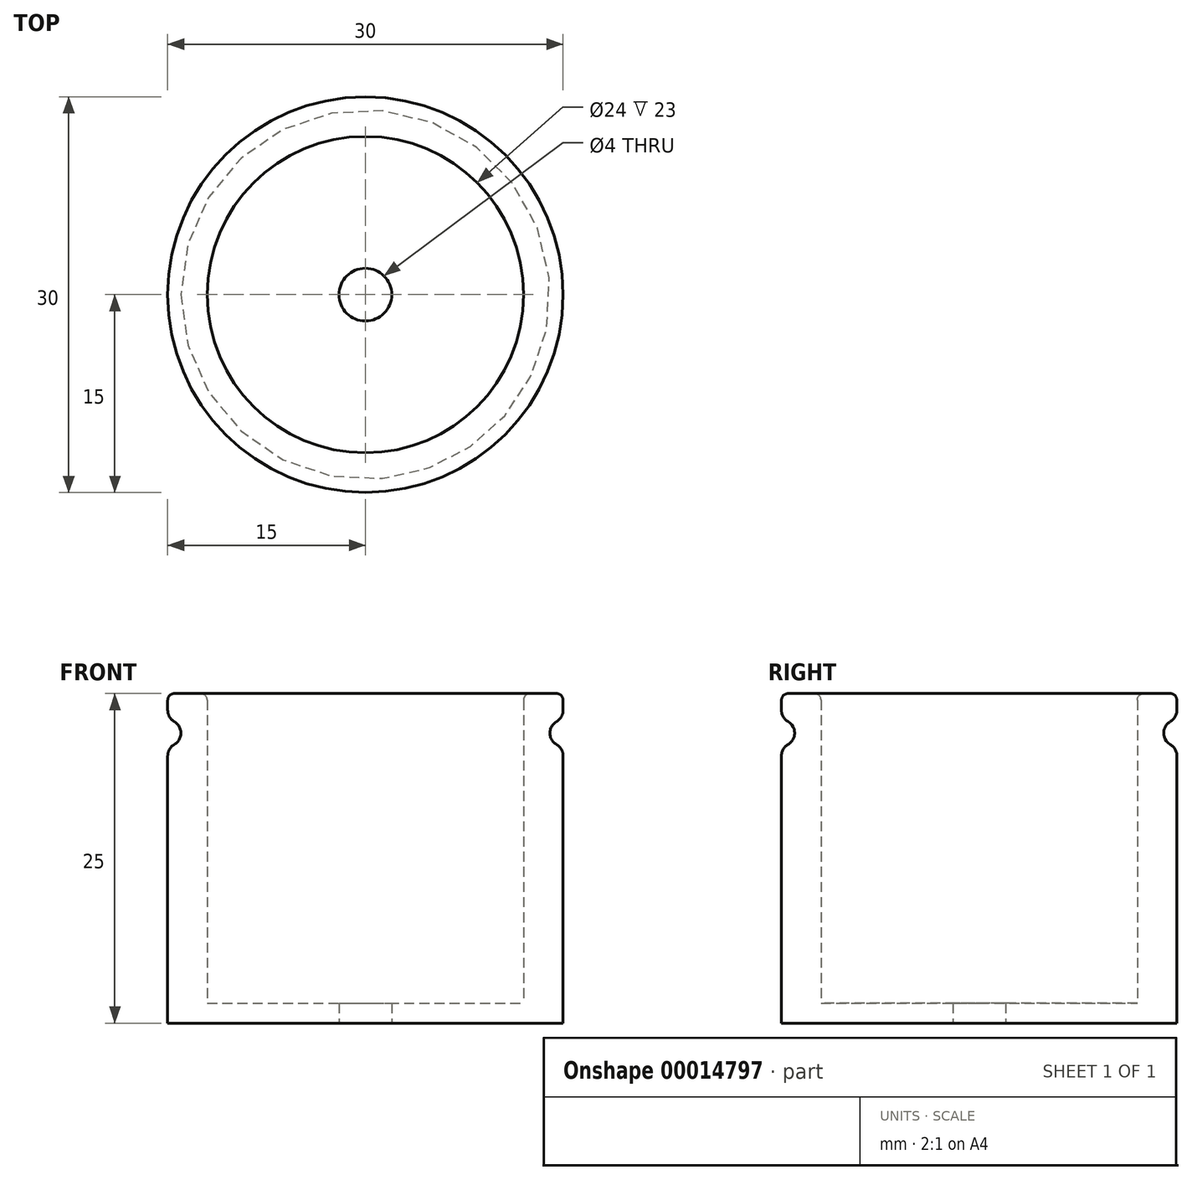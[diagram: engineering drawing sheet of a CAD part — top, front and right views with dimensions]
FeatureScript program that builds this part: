
annotation { "Feature Type Name" : "Feature", "Feature Type Description" : "" }
export const myFeature = defineFeature(function(context is Context, id is Id, definition is map)
    precondition{}
    {
        {
            var Q0;
            Q0=qCreatedBy(makeId("Front.planeOp"),FACE);
            var sketch = newSketch(context, id + "F0", { "sketchPlane" : qUnion([Q0])});
            skLineSegment(sketch, "E0.top", {"start": v(2, 1.5) * mm, "end": v(12, 1.5) * mm});
            skLineSegment(sketch, "E0.left", {"start": v(2, 0) * mm, "end": v(2, 1.5) * mm});
            skLineSegment(sketch, "E1.top", {"start": v(15, 25) * mm, "end": v(12, 25) * mm});
            skLineSegment(sketch, "E1.left", {"start": v(15, 0) * mm, "end": v(15, 25) * mm});
            skLineSegment(sketch, "E1.right", {"start": v(12, 1.5) * mm, "end": v(12, 25) * mm});
            skLineSegment(sketch, "E2", {"start": v(2, 0) * mm, "end": v(15, 0) * mm});
            skLineSegment(sketch, "E3", {"start": v(0, 0) * mm, "end": v(0, 24.75) * mm, "construction": true});
            skSolve(sketch);
        }
        {
            var Q0;
            Q0 = qSketchRegion(id + "F0", true);
            var Q1;
            Q1=sQuery(id+"F0.wireOp",EDGE,"E3");
            revolve(context, id + "F1", {"entities" : qUnion([Q0]), "axis" : qUnion([Q1]), "revolveType" : RevolveType.FULL});
        }
        {
            var Q0;
            Q0=qCreatedBy(makeId("Front.planeOp"),FACE);
            var sketch = newSketch(context, id + "F2", { "sketchPlane" : qUnion([Q0])});
            skCircle(sketch, "E4", {"center": v(15, 22) * mm, "radius": 1 * mm});
            skSolve(sketch);
        }
        {
            var Q0;
            Q0 = qSketchRegion(id + "F2", true);
            var Q1;
            Q1=makeQuery(id+"F1.opRevolve","SWEPT_FACE",FACE,{"disambiguationData":[OSD([sQuery(id+"F0.wireOp",EDGE,"E1.left")])]});
            revolve(context, id + "F3", {"operationType" : NewBodyOperationType.REMOVE, "entities" : qUnion([Q0]), "axis" : qUnion([Q1]), "revolveType" : RevolveType.FULL, "oppositeDirection" : true});
        }
        {
            var Q0;
            Q0=makeQuery(id+"F3.boolean.opBoolean","INTERSECT",EDGE,{"disambiguationData":[OD(0.0)],"derivedFrom":[makeQuery(id+"F1.opRevolve","SWEPT_FACE",FACE,{"disambiguationData":[OSD([sQuery(id+"F0.wireOp",EDGE,"E1.left")])]}),makeQuery(id+"F3.opRevolve","SWEPT_FACE",FACE,{"disambiguationData":[OSD([sQuery(id+"F2.wireOp",EDGE,"E4")])]})]});
            var Q1;
            Q1=makeQuery(id+"F3.boolean.opBoolean","INTERSECT",EDGE,{"disambiguationData":[OD(1.0)],"derivedFrom":[makeQuery(id+"F1.opRevolve","SWEPT_FACE",FACE,{"disambiguationData":[OSD([sQuery(id+"F0.wireOp",EDGE,"E1.left")])]}),makeQuery(id+"F3.opRevolve","SWEPT_FACE",FACE,{"disambiguationData":[OSD([sQuery(id+"F2.wireOp",EDGE,"E4")])]})]});
            fillet(context, id + "F4", {"entities" : qUnion([Q0, Q1]), "radius" : 1 * mm, "tangentPropagation" : true, "allowEdgeOverflow" : false});
        }
        {
            var Q0;
            Q0=makeQuery(id+"F1.opRevolve","SWEPT_FACE",FACE,{"disambiguationData":[OSD([sQuery(id+"F0.wireOp",EDGE,"E1.top")])]});
            fillet(context, id + "F5", {"entities" : qUnion([Q0]), "radius" : 0.5 * mm, "tangentPropagation" : true, "allowEdgeOverflow" : false});
        }
    });
